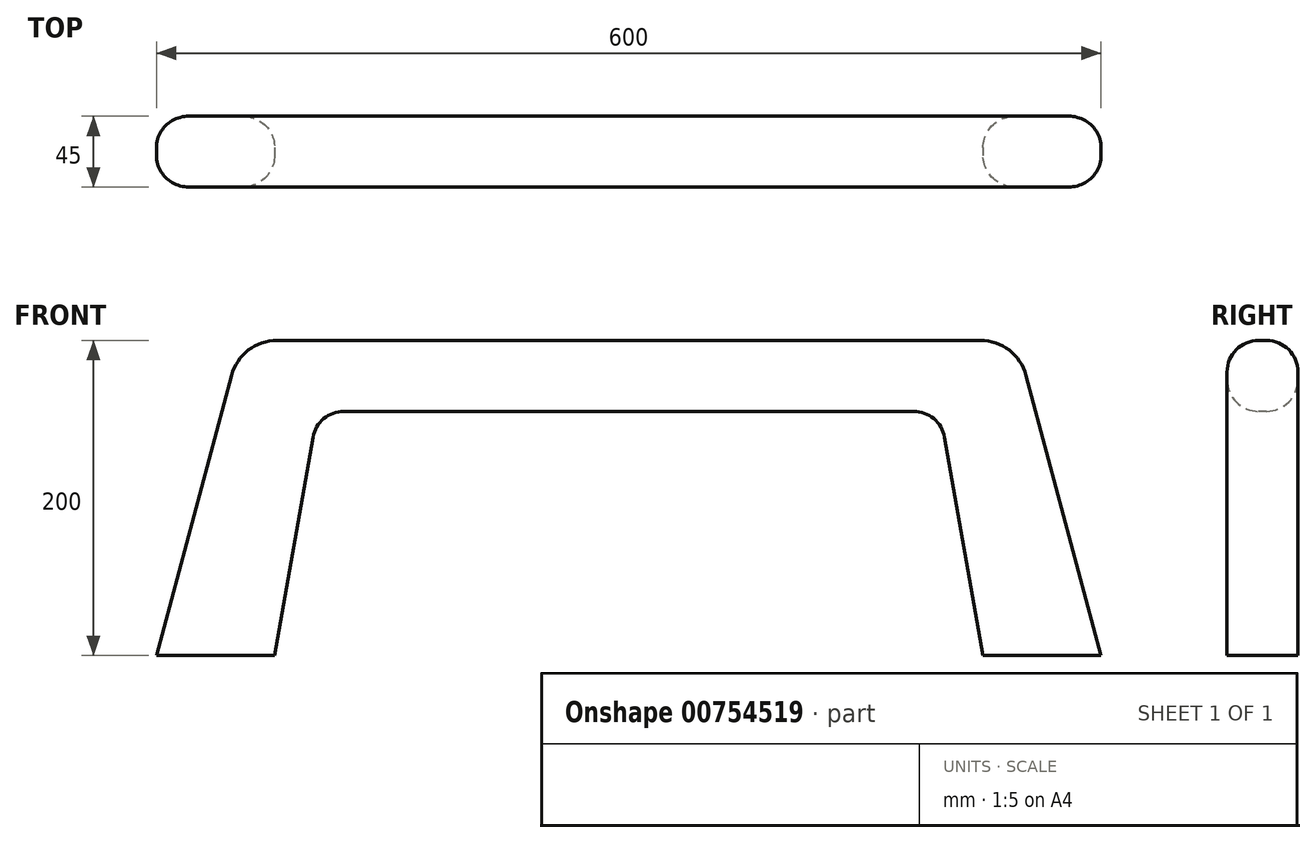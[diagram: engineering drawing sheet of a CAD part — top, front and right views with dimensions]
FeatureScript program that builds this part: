
annotation { "Feature Type Name" : "Feature", "Feature Type Description" : "" }
export const myFeature = defineFeature(function(context is Context, id is Id, definition is map)
    precondition{}
    {
        {
            var Q0;
            Q0=qCreatedBy(makeId("Front.planeOp"),FACE);
            var sketch = newSketch(context, id + "F0", { "sketchPlane" : qUnion([Q0])});
            skLineSegment(sketch, "E0", {"start": v(-300, 0) * mm, "end": v(-246.41, 200) * mm});
            skLineSegment(sketch, "E1", {"start": v(-246.41, 200) * mm, "end": v(246.41, 200) * mm});
            skLineSegment(sketch, "E2", {"start": v(-300, 0) * mm, "end": v(-225, 0) * mm});
            skLineSegment(sketch, "E3", {"start": v(300, 0) * mm, "end": v(246.41, 200) * mm});
            skLineSegment(sketch, "E4", {"start": v(-197.67, 155) * mm, "end": v(-225, 0) * mm});
            skLineSegment(sketch, "E5", {"start": v(-197.67, 155) * mm, "end": v(197.67, 155) * mm});
            skLineSegment(sketch, "E6", {"start": v(197.67, 155) * mm, "end": v(225, 0) * mm});
            skLineSegment(sketch, "E7.trimOffspring", {"start": v(225, 0) * mm, "end": v(300, 0) * mm});
            skSolve(sketch);
        }
        {
            var Q0;
            Q0 = qSketchRegion(id + "F0", true);
            extrude(context, id + "F1", {"entities" : qUnion([Q0]), "endBound" : BoundingType.SYMMETRIC, "oppositeDirection" : true, "depth" : (15 * 3) * mm, "offsetDistance" : 25 * mm});
        }
        {
            var Q0;
            Q0=makeQuery(id+"F1.opExtrude","SWEPT_EDGE",EDGE,{"disambiguationData":[OSD([sQuery(id+"F0.wireOp",EDGE,"E1"),sQuery(id+"F0.wireOp",EDGE,"E3")])]});
            var Q1;
            Q1=makeQuery(id+"F1.opExtrude","SWEPT_EDGE",EDGE,{"disambiguationData":[OSD([sQuery(id+"F0.wireOp",EDGE,"E0"),sQuery(id+"F0.wireOp",EDGE,"E1")])]});
            fillet(context, id + "F2", {"entities" : qUnion([Q0, Q1]), "radius" : 30 * mm, "tangentPropagation" : true, "allowEdgeOverflow" : false});
        }
        {
            var Q0;
            Q0=makeQuery(id+"F1.opExtrude","SWEPT_EDGE",EDGE,{"disambiguationData":[OSD([sQuery(id+"F0.wireOp",EDGE,"E4"),sQuery(id+"F0.wireOp",EDGE,"E5")])]});
            var Q1;
            Q1=makeQuery(id+"F1.opExtrude","SWEPT_EDGE",EDGE,{"disambiguationData":[OSD([sQuery(id+"F0.wireOp",EDGE,"E5"),sQuery(id+"F0.wireOp",EDGE,"E6")])]});
            fillet(context, id + "F3", {"entities" : qUnion([Q0, Q1]), "radius" : 20 * mm, "tangentPropagation" : true, "allowEdgeOverflow" : false});
        }
        {
            var Q0;
            Q0=makeQuery(id+"F1.opExtrude","CAP_EDGE",EDGE,{"disambiguationData":[OSD([sQuery(id+"F0.wireOp",EDGE,"E1")])],"isStart":true});
            var Q1;
            Q1=makeQuery(id+"F1.opExtrude","CAP_EDGE",EDGE,{"disambiguationData":[OSD([sQuery(id+"F0.wireOp",EDGE,"E5")])],"isStart":true});
            var Q2;
            Q2=makeQuery(id+"F1.opExtrude","CAP_EDGE",EDGE,{"disambiguationData":[OSD([sQuery(id+"F0.wireOp",EDGE,"E6")])],"isStart":false});
            var Q3;
            Q3=makeQuery(id+"F1.opExtrude","CAP_EDGE",EDGE,{"disambiguationData":[OSD([sQuery(id+"F0.wireOp",EDGE,"E3")])],"isStart":false});
            fillet(context, id + "F4", {"entities" : qUnion([Q0, Q1, Q2, Q3]), "radius" : 20 * mm, "tangentPropagation" : true, "allowEdgeOverflow" : false});
        }
    });
